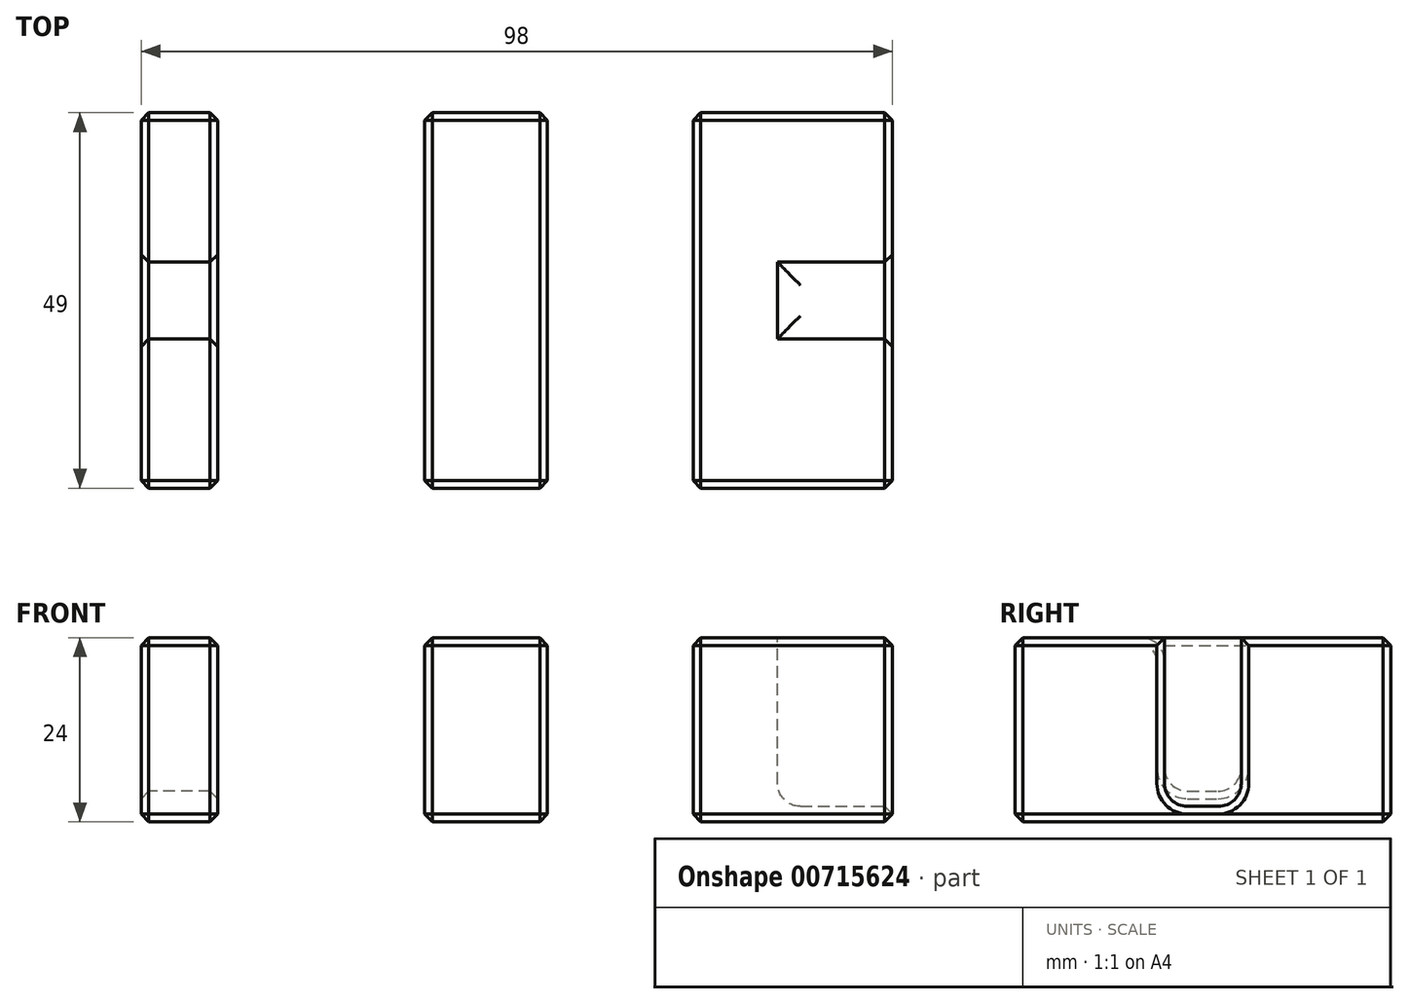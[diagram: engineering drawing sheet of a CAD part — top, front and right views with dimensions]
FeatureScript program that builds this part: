
annotation { "Feature Type Name" : "Feature", "Feature Type Description" : "" }
export const myFeature = defineFeature(function(context is Context, id is Id, definition is map)
    precondition{}
    {
        {
            var Q0;
            Q0=qCreatedBy(makeId("Top.planeOp"),FACE);
            var sketch = newSketch(context, id + "F0", { "sketchPlane" : qUnion([Q0])});
            skLineSegment(sketch, "E0.bottom", {"start": v(-8, -24.5) * mm, "end": v(8, -24.5) * mm});
            skLineSegment(sketch, "E0.top", {"start": v(-8, 24.5) * mm, "end": v(8, 24.5) * mm});
            skLineSegment(sketch, "E0.left", {"start": v(-8, -24.5) * mm, "end": v(-8, 24.5) * mm});
            skLineSegment(sketch, "E0.right", {"start": v(8, -24.5) * mm, "end": v(8, 24.5) * mm});
            skPoint(sketch, "E0.middle", {"position": v(0, 0) * mm});
            skLineSegment(sketch, "E1", {"start": v(0, 0) * mm, "end": v(40, 0) * mm, "construction": true});
            skLineSegment(sketch, "E2.bottom", {"start": v(27, 24.5) * mm, "end": v(53, 24.5) * mm});
            skLineSegment(sketch, "E2.top", {"start": v(27, -24.5) * mm, "end": v(53, -24.5) * mm});
            skLineSegment(sketch, "E2.left", {"start": v(27, 24.5) * mm, "end": v(27, -24.5) * mm});
            skLineSegment(sketch, "E2.right", {"start": v(53, 24.5) * mm, "end": v(53, -24.5) * mm});
            skPoint(sketch, "E2.middle", {"position": v(40, 0) * mm});
            skLineSegment(sketch, "E3", {"start": v(0, 0) * mm, "end": v(-40, 0) * mm, "construction": true});
            skLineSegment(sketch, "E4.bottom", {"start": v(-45, -24.5) * mm, "end": v(-35, -24.5) * mm});
            skLineSegment(sketch, "E4.top", {"start": v(-45, 24.5) * mm, "end": v(-35, 24.5) * mm});
            skLineSegment(sketch, "E4.left", {"start": v(-45, -24.5) * mm, "end": v(-45, 24.5) * mm});
            skLineSegment(sketch, "E4.right", {"start": v(-35, -24.5) * mm, "end": v(-35, 24.5) * mm});
            skPoint(sketch, "E4.middle", {"position": v(-40, 0) * mm});
            skSolve(sketch);
        }
        {
            var Q0;
            Q0=makeQuery(id+"F0.imprint","IMPRINT",FACE,{"disambiguationData":[TD([[makeQuery(id+"F0.imprint","IMPRINT",EDGE,{"derivedFrom":sQuery(id+"F0.wireOp",EDGE,"E0.bottom")}),1.0]])]});
            extrude(context, id + "F1", {"entities" : qUnion([Q0]), "depth" : 24 * mm, "offsetDistance" : 25 * mm});
        }
        {
            var Q0;
            Q0=makeQuery(id+"F1.opExtrude","CAP_FACE",FACE,{"disambiguationData":[OSD([sQuery(id+"F0.wireOp",EDGE,"E0.bottom"),sQuery(id+"F0.wireOp",EDGE,"E0.top"),sQuery(id+"F0.wireOp",EDGE,"E0.left"),sQuery(id+"F0.wireOp",EDGE,"E0.right")])],"isStart":true});
            var Q1;
            Q1=makeQuery(id+"F1.opExtrude","SWEPT_EDGE",EDGE,{"disambiguationData":[OSD([sQuery(id+"F0.wireOp",EDGE,"E0.bottom"),sQuery(id+"F0.wireOp",EDGE,"E0.right")])]});
            var Q2;
            Q2=makeQuery(id+"F1.opExtrude","SWEPT_EDGE",EDGE,{"disambiguationData":[OSD([sQuery(id+"F0.wireOp",EDGE,"E0.top"),sQuery(id+"F0.wireOp",EDGE,"E0.right")])]});
            var Q3;
            Q3=makeQuery(id+"F1.opExtrude","SWEPT_EDGE",EDGE,{"disambiguationData":[OSD([sQuery(id+"F0.wireOp",EDGE,"E0.top"),sQuery(id+"F0.wireOp",EDGE,"E0.left")])]});
            var Q4;
            Q4=makeQuery(id+"F1.opExtrude","SWEPT_EDGE",EDGE,{"disambiguationData":[OSD([sQuery(id+"F0.wireOp",EDGE,"E0.bottom"),sQuery(id+"F0.wireOp",EDGE,"E0.left")])]});
            var Q5;
            Q5=makeQuery(id+"F1.opExtrude","CAP_FACE",FACE,{"disambiguationData":[OSD([sQuery(id+"F0.wireOp",EDGE,"E0.bottom"),sQuery(id+"F0.wireOp",EDGE,"E0.top"),sQuery(id+"F0.wireOp",EDGE,"E0.left"),sQuery(id+"F0.wireOp",EDGE,"E0.right")])],"isStart":false});
            chamfer(context, id + "F2", {"entities" : qUnion([Q0, Q1, Q2, Q3, Q4, Q5]), "width" : 1 * mm, "tangentPropagation" : true});
        }
        {
            var Q0;
            Q0=makeQuery(id+"F0.imprint","IMPRINT",FACE,{"disambiguationData":[TD([[makeQuery(id+"F0.imprint","IMPRINT",EDGE,{"derivedFrom":sQuery(id+"F0.wireOp",EDGE,"E2.bottom")}),-1.0]])]});
            extrude(context, id + "F3", {"entities" : qUnion([Q0]), "depth" : 24 * mm, "offsetDistance" : 25 * mm});
        }
        {
            var Q0;
            Q0=makeQuery(id+"F3.opExtrude","SWEPT_FACE",FACE,{"disambiguationData":[OSD([sQuery(id+"F0.wireOp",EDGE,"E2.right")])]});
            var sketch = newSketch(context, id + "F4", { "sketchPlane" : qUnion([Q0])});
            skLineSegment(sketch, "E5", {"start": v(0, 0) * mm, "end": v(0, 24) * mm, "construction": true});
            skLineSegment(sketch, "E6", {"start": v(0, 0) * mm, "end": v(0, 2) * mm, "construction": true});
            skLineSegment(sketch, "E7", {"start": v(0, 2) * mm, "end": v(-5, 2) * mm});
            skLineSegment(sketch, "E8", {"start": v(-5, 2) * mm, "end": v(-5, 24) * mm});
            skLineSegment(sketch, "E9.MirrorCS", {"start": v(0, 2) * mm, "end": v(5, 2) * mm});
            skLineSegment(sketch, "E10.MirrorCS", {"start": v(5, 2) * mm, "end": v(5, 24) * mm});
            skSolve(sketch);
        }
        {
            var Q0;
            Q0=makeQuery(id+"F4.imprint","IMPRINT",FACE,{"disambiguationData":[TD([[makeQuery(id+"F4.imprint","IMPRINT",EDGE,{"derivedFrom":sQuery(id+"F4.wireOp",EDGE,"E7")}),-1.0]])]});
            extrude(context, id + "F5", {"entities" : qUnion([Q0]), "operationType" : NewBodyOperationType.REMOVE, "oppositeDirection" : true, "depth" : 15 * mm, "offsetDistance" : 25 * mm});
        }
        {
            var Q0;
            Q0=makeQuery(id+"F0.imprint","IMPRINT",FACE,{"disambiguationData":[TD([[makeQuery(id+"F0.imprint","IMPRINT",EDGE,{"derivedFrom":sQuery(id+"F0.wireOp",EDGE,"E4.bottom")}),1.0]])]});
            extrude(context, id + "F6", {"entities" : qUnion([Q0]), "depth" : 24 * mm, "offsetDistance" : 25 * mm});
        }
        {
            var Q0;
            Q0=makeQuery(id+"F6.opExtrude","SWEPT_FACE",FACE,{"disambiguationData":[OSD([sQuery(id+"F0.wireOp",EDGE,"E4.left")])]});
            var sketch = newSketch(context, id + "F7", { "sketchPlane" : qUnion([Q0])});
            skLineSegment(sketch, "E11", {"start": v(0, 0) * mm, "end": v(0, 24) * mm, "construction": true});
            skLineSegment(sketch, "E12", {"start": v(0, 0) * mm, "end": v(0, 4) * mm, "construction": true});
            skLineSegment(sketch, "E13", {"start": v(0, 4) * mm, "end": v(-5, 4) * mm});
            skLineSegment(sketch, "E14", {"start": v(-5, 4) * mm, "end": v(-5, 24) * mm});
            skLineSegment(sketch, "E15.MirrorCS", {"start": v(0, 4) * mm, "end": v(5, 4) * mm});
            skLineSegment(sketch, "E16.MirrorCS", {"start": v(5, 4) * mm, "end": v(5, 24) * mm});
            skSolve(sketch);
        }
        {
            var Q0;
            Q0=makeQuery(id+"F7.imprint","IMPRINT",FACE,{"disambiguationData":[TD([[makeQuery(id+"F7.imprint","IMPRINT",EDGE,{"derivedFrom":sQuery(id+"F7.wireOp",EDGE,"E13")}),-1.0]])]});
            extrude(context, id + "F8", {"entities" : qUnion([Q0]), "operationType" : NewBodyOperationType.REMOVE, "oppositeDirection" : true, "depth" : 26 * mm, "offsetDistance" : 25 * mm});
        }
        {
            var Q0;
            Q0=makeQuery(id+"F5.boolean.opBoolean","COPY",EDGE,{"derivedFrom":makeQuery(id+"F5.opExtrude","SWEPT_EDGE",EDGE,{"disambiguationData":[OSD([sQuery(id+"F4.wireOp",EDGE,"E9.MirrorCS"),sQuery(id+"F4.wireOp",EDGE,"E10.MirrorCS")])]})});
            var Q1;
            Q1=makeQuery(id+"F5.boolean.opBoolean","COPY",EDGE,{"derivedFrom":makeQuery(id+"F5.opExtrude","SWEPT_EDGE",EDGE,{"disambiguationData":[OSD([sQuery(id+"F4.wireOp",EDGE,"E7"),sQuery(id+"F4.wireOp",EDGE,"E8")])]})});
            var Q2;
            Q2=makeQuery(id+"F5.boolean.opBoolean","COPY",EDGE,{"derivedFrom":makeQuery(id+"F5.opExtrude","CAP_EDGE",EDGE,{"disambiguationData":[OSD([sQuery(id+"F4.wireOp",EDGE,"E7"),sQuery(id+"F4.wireOp",EDGE,"E9.MirrorCS")])],"isStart":false})});
            var Q3;
            Q3=makeQuery(id+"F5.boolean.opBoolean","COPY",EDGE,{"derivedFrom":makeQuery(id+"F5.opExtrude","SWEPT_EDGE",EDGE,{"disambiguationData":[OSD([sQuery(id+"F0.wireOp",EDGE,"E2.right"),sQuery(id+"F4.wireOp",EDGE,"E10.MirrorCS")])]})});
            var Q4;
            Q4=makeQuery(id+"F5.boolean.opBoolean","COPY",EDGE,{"derivedFrom":makeQuery(id+"F5.opExtrude","CAP_EDGE",EDGE,{"disambiguationData":[OSD([sQuery(id+"F0.wireOp",EDGE,"E2.right")])],"isStart":false})});
            var Q5;
            Q5=makeQuery(id+"F5.boolean.opBoolean","COPY",EDGE,{"derivedFrom":makeQuery(id+"F5.opExtrude","SWEPT_EDGE",EDGE,{"disambiguationData":[OSD([sQuery(id+"F0.wireOp",EDGE,"E2.right"),sQuery(id+"F4.wireOp",EDGE,"E8")])]})});
            var Q6;
            Q6=makeQuery(id+"F8.boolean.opBoolean","COPY",EDGE,{"derivedFrom":makeQuery(id+"F8.opExtrude","SWEPT_EDGE",EDGE,{"disambiguationData":[OSD([sQuery(id+"F7.wireOp",EDGE,"E15.MirrorCS"),sQuery(id+"F7.wireOp",EDGE,"E16.MirrorCS")])]})});
            var Q7;
            Q7=makeQuery(id+"F8.boolean.opBoolean","COPY",EDGE,{"derivedFrom":makeQuery(id+"F8.opExtrude","SWEPT_EDGE",EDGE,{"disambiguationData":[OSD([sQuery(id+"F7.wireOp",EDGE,"E13"),sQuery(id+"F7.wireOp",EDGE,"E14")])]})});
            var Q8;
            Q8=makeQuery(id+"F8.boolean.opBoolean","COPY",EDGE,{"derivedFrom":makeQuery(id+"F8.opExtrude","SWEPT_EDGE",EDGE,{"disambiguationData":[OSD([sQuery(id+"F0.wireOp",EDGE,"E4.left"),sQuery(id+"F7.wireOp",EDGE,"E14")])]})});
            var Q9;
            Q9=makeQuery(id+"F8.boolean.opBoolean","COPY",EDGE,{"derivedFrom":makeQuery(id+"F8.opExtrude","SWEPT_EDGE",EDGE,{"disambiguationData":[OSD([sQuery(id+"F0.wireOp",EDGE,"E4.left"),sQuery(id+"F7.wireOp",EDGE,"E16.MirrorCS")])]})});
            fillet(context, id + "F9", {"entities" : qUnion([Q0, Q1, Q2, Q3, Q4, Q5, Q6, Q7, Q8, Q9]), "radius" : 3 * mm, "tangentPropagation" : true, "allowEdgeOverflow" : false});
        }
        {
            var Q0;
            Q0=makeQuery(id+"F3.opExtrude","SWEPT_FACE",FACE,{"disambiguationData":[OSD([sQuery(id+"F0.wireOp",EDGE,"E2.right")])]});
            var Q1;
            Q1=makeQuery(id+"F3.opExtrude","SWEPT_FACE",FACE,{"disambiguationData":[OSD([sQuery(id+"F0.wireOp",EDGE,"E2.top")])]});
            var Q2;
            Q2=makeQuery(id+"F3.opExtrude","SWEPT_FACE",FACE,{"disambiguationData":[OSD([sQuery(id+"F0.wireOp",EDGE,"E2.left")])]});
            var Q3;
            Q3=makeQuery(id+"F3.opExtrude","CAP_FACE",FACE,{"disambiguationData":[OSD([sQuery(id+"F0.wireOp",EDGE,"E2.bottom"),sQuery(id+"F0.wireOp",EDGE,"E2.top"),sQuery(id+"F0.wireOp",EDGE,"E2.left"),sQuery(id+"F0.wireOp",EDGE,"E2.right")])],"isStart":true});
            var Q4;
            Q4=makeQuery(id+"F3.opExtrude","SWEPT_FACE",FACE,{"disambiguationData":[OSD([sQuery(id+"F0.wireOp",EDGE,"E2.bottom")])]});
            var Q5;
            Q5=makeQuery(id+"F6.opExtrude","SWEPT_FACE",FACE,{"disambiguationData":[OSD([sQuery(id+"F0.wireOp",EDGE,"E4.left")])]});
            var Q6;
            Q6=makeQuery(id+"F6.opExtrude","SWEPT_FACE",FACE,{"disambiguationData":[OSD([sQuery(id+"F0.wireOp",EDGE,"E4.right")])]});
            var Q7;
            Q7=makeQuery(id+"F6.opExtrude","CAP_FACE",FACE,{"disambiguationData":[OSD([sQuery(id+"F0.wireOp",EDGE,"E4.bottom"),sQuery(id+"F0.wireOp",EDGE,"E4.top"),sQuery(id+"F0.wireOp",EDGE,"E4.left"),sQuery(id+"F0.wireOp",EDGE,"E4.right")])],"isStart":true});
            var Q8;
            Q8=makeQuery(id+"F6.opExtrude","SWEPT_FACE",FACE,{"disambiguationData":[OSD([sQuery(id+"F0.wireOp",EDGE,"E4.top")])]});
            var Q9;
            Q9=makeQuery(id+"F6.opExtrude","SWEPT_FACE",FACE,{"disambiguationData":[OSD([sQuery(id+"F0.wireOp",EDGE,"E4.bottom")])]});
            chamfer(context, id + "F10", {"entities" : qUnion([Q0, Q1, Q2, Q3, Q4, Q5, Q6, Q7, Q8, Q9]), "width" : 1 * mm, "tangentPropagation" : true});
        }
    });
